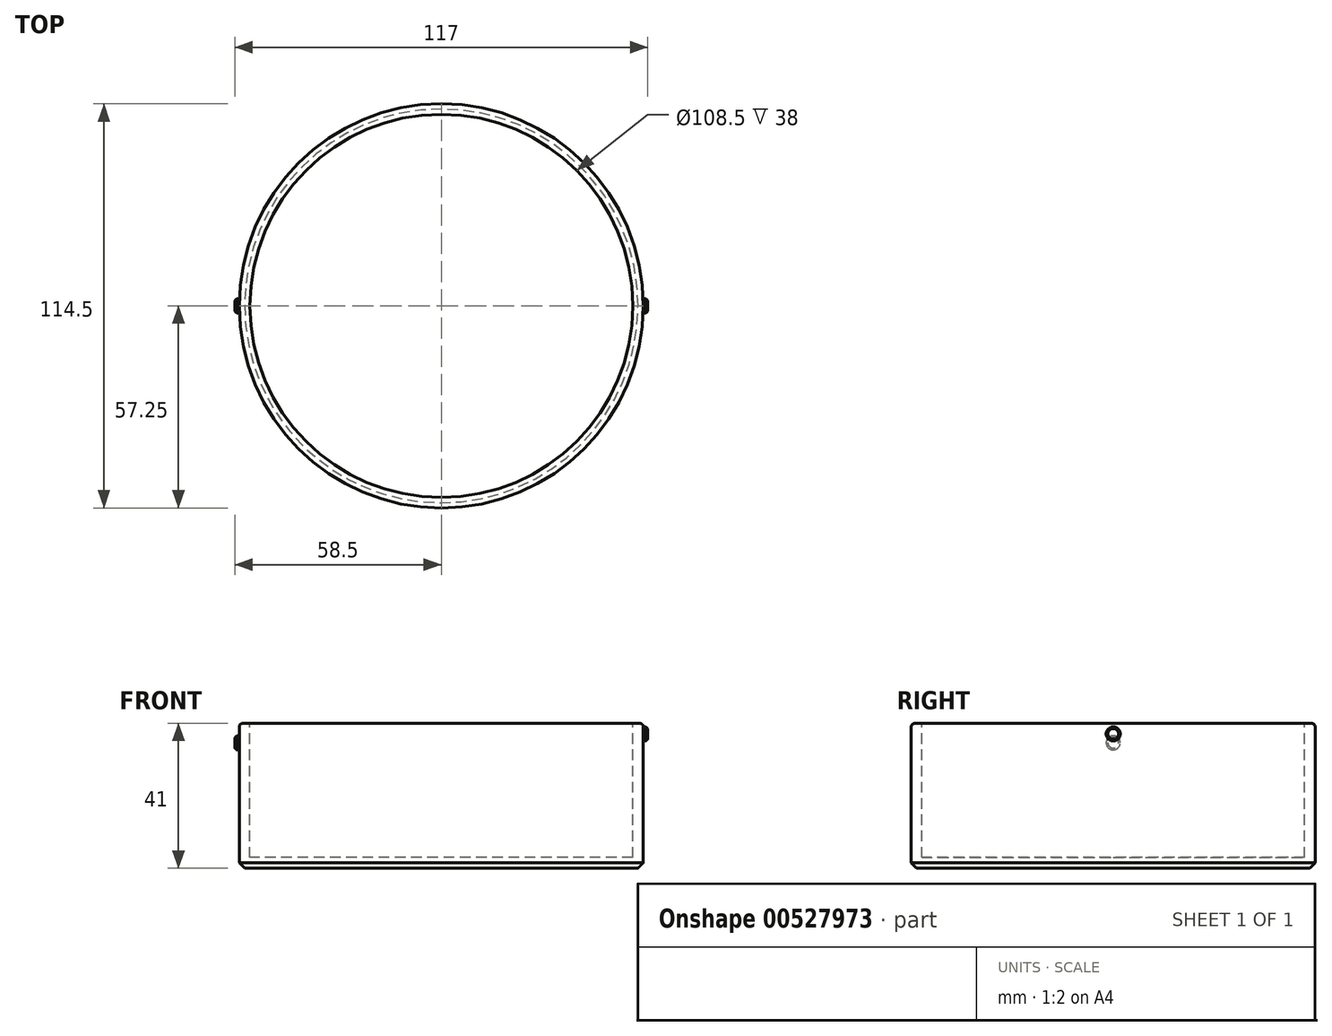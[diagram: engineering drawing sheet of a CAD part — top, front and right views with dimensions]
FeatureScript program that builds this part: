
annotation { "Feature Type Name" : "Feature", "Feature Type Description" : "" }
export const myFeature = defineFeature(function(context is Context, id is Id, definition is map)
    precondition{}
    {
        {
            var Q0;
            Q0=qCreatedBy(makeId("Top.planeOp"),FACE);
            var sketch = newSketch(context, id + "F0", { "sketchPlane" : qUnion([Q0])});
            skCircle(sketch, "E0", {"center": v(0, 0) * mm, "radius": 57.25 * mm});
            skSolve(sketch);
        }
        {
            var Q0;
            Q0 = qSketchRegion(id + "F0", true);
            extrude(context, id + "F1", {"entities" : qUnion([Q0]), "depth" : (38 + 3) * mm, "offsetDistance" : 25 * mm});
        }
        {
            var Q0;
            Q0=makeQuery(id+"F1.opExtrude","CAP_FACE",FACE,{"disambiguationData":[OSD([sQuery(id+"F0.wireOp",EDGE,"E0")])],"isStart":false});
            var sketch = newSketch(context, id + "F2", { "sketchPlane" : qUnion([Q0])});
            skCircle(sketch, "E1", {"center": v(0, 0) * mm, "radius": 54.25 * mm});
            skSolve(sketch);
        }
        {
            var Q0;
            Q0 = qSketchRegion(id + "F2", true);
            extrude(context, id + "F3", {"entities" : qUnion([Q0]), "operationType" : NewBodyOperationType.REMOVE, "oppositeDirection" : true, "depth" : 38 * mm, "offsetDistance" : 25 * mm});
        }
        {
            var Q0;
            Q0=qCreatedBy(makeId("Right.planeOp"),FACE);
            var sketch = newSketch(context, id + "F4", { "sketchPlane" : qUnion([Q0])});
            skCircle(sketch, "E2", {"center": v(0, 38) * mm, "radius": 2 * mm});
            skSolve(sketch);
        }
        {
            var Q0;
            Q0 = qSketchRegion(id + "F4", true);
            var Q1;
            Q1=makeQuery(id+"F3.boolean.opBoolean","COPY",FACE,{"derivedFrom":makeQuery(id+"F3.opExtrude","SWEPT_FACE",FACE,{"disambiguationData":[OSD([sQuery(id+"F2.wireOp",EDGE,"E1")])]})});
            extrude(context, id + "F5", {"entities" : qUnion([Q0]), "operationType" : NewBodyOperationType.ADD, "depth" : 58.5 * mm, "offsetDistance" : 25 * mm, "hasSecondDirection" : true, "secondDirectionBound" : SecondDirectionBoundingType.UP_TO_SURFACE, "secondDirectionOppositeDirection" : false, "secondDirectionDepth" : 56.4 * mm, "secondDirectionBoundEntityFace" : qUnion([Q1])});
        }
        {
            var Q0;
            Q0=makeQuery(id+"F5.opExtrude","CAP_FACE",FACE,{"disambiguationData":[OSD([sQuery(id+"F4.wireOp",EDGE,"E2")])],"isStart":false});
            chamfer(context, id + "F6", {"entities" : qUnion([Q0]), "width" : 0.5 * mm});
        }
        {
            var Q0;
            Q0=qCreatedBy(makeId("Right.planeOp"),FACE);
            var sketch = newSketch(context, id + "F7", { "sketchPlane" : qUnion([Q0])});
            skCircle(sketch, "E3", {"center": v(0, 35.5) * mm, "radius": 2 * mm});
            skSolve(sketch);
        }
        {
            var Q0;
            Q0 = qSketchRegion(id + "F7", true);
            var Q1;
            Q1=makeQuery(id+"F3.boolean.opBoolean","COPY",FACE,{"derivedFrom":makeQuery(id+"F3.opExtrude","SWEPT_FACE",FACE,{"disambiguationData":[OSD([sQuery(id+"F2.wireOp",EDGE,"E1")])]})});
            extrude(context, id + "F8", {"entities" : qUnion([Q0]), "operationType" : NewBodyOperationType.ADD, "oppositeDirection" : true, "depth" : 58.5 * mm, "offsetDistance" : 25 * mm, "hasSecondDirection" : true, "secondDirectionBound" : SecondDirectionBoundingType.UP_TO_SURFACE, "secondDirectionOppositeDirection" : true, "secondDirectionDepth" : 25 * mm, "secondDirectionBoundEntityFace" : qUnion([Q1])});
        }
        {
            var Q0;
            Q0=makeQuery(id+"F8.opExtrude","CAP_EDGE",EDGE,{"disambiguationData":[OSD([sQuery(id+"F7.wireOp",EDGE,"E3")])],"isStart":false});
            chamfer(context, id + "F9", {"entities" : qUnion([Q0]), "width" : 0.5 * mm, "tangentPropagation" : true});
        }
        {
            var Q0;
            Q0=makeQuery(id+"F1.opExtrude","CAP_EDGE",EDGE,{"disambiguationData":[OSD([sQuery(id+"F0.wireOp",EDGE,"E0")])],"isStart":false});
            fillet(context, id + "F10", {"entities" : qUnion([Q0]), "radius" : 1 * mm, "tangentPropagation" : true, "allowEdgeOverflow" : false});
        }
        {
            var Q0;
            Q0=makeQuery(id+"F1.opExtrude","CAP_EDGE",EDGE,{"disambiguationData":[OSD([sQuery(id+"F0.wireOp",EDGE,"E0")])],"isStart":true});
            chamfer(context, id + "F11", {"entities" : qUnion([Q0]), "width" : 1.5 * mm, "tangentPropagation" : true});
        }
    });
